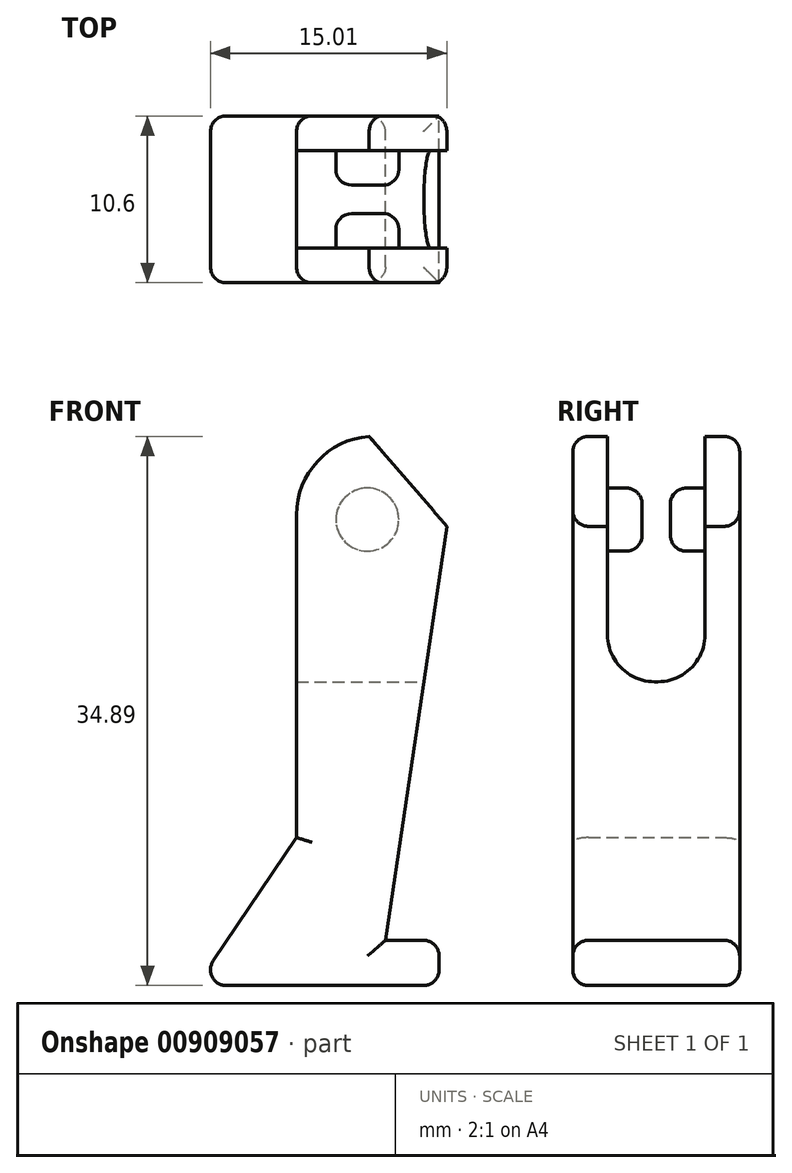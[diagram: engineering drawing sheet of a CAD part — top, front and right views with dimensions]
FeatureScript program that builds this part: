
annotation { "Feature Type Name" : "Feature", "Feature Type Description" : "" }
export const myFeature = defineFeature(function(context is Context, id is Id, definition is map)
    precondition{}
    {
        {
            var Q0;
            Q0=qCreatedBy(makeId("Front.planeOp"),FACE);
            var sketch = newSketch(context, id + "F0", { "sketchPlane" : qUnion([Q0])});
            skLineSegment(sketch, "E0", {"start": v(-7.7, 0) * mm, "end": v(7.7, 0) * mm});
            skLineSegment(sketch, "E1", {"start": v(-7.7, 0) * mm, "end": v(-1.36, 9.4) * mm});
            skLineSegment(sketch, "E2", {"start": v(-1.36, 9.4) * mm, "end": v(-1.36, 34.9) * mm});
            skLineSegment(sketch, "E3", {"start": v(-1.36, 34.9) * mm, "end": v(9.04, 34.9) * mm});
            skLineSegment(sketch, "E4", {"start": v(7.7, 0) * mm, "end": v(7.7, 2.88) * mm});
            skLineSegment(sketch, "E5", {"start": v(7.7, 2.88) * mm, "end": v(4.3, 2.88) * mm});
            skLineSegment(sketch, "E6", {"start": v(4.3, 2.88) * mm, "end": v(9.04, 34.9) * mm});
            skSolve(sketch);
        }
        {
            var Q0;
            Q0=makeQuery(id+"F0.imprint","IMPRINT",FACE,{"disambiguationData":[TD([[makeQuery(id+"F0.imprint","IMPRINT",EDGE,{"derivedFrom":sQuery(id+"F0.wireOp",EDGE,"E0")}),1.0]])]});
            extrude(context, id + "F1", {"entities" : qUnion([Q0]), "depth" : 10.6 * mm, "offsetDistance" : 25 * mm});
        }
        {
            var Q0;
            Q0=makeQuery(id+"F1.opExtrude","SWEPT_EDGE",EDGE,{"disambiguationData":[OSD([sQuery(id+"F0.wireOp",EDGE,"E2"),sQuery(id+"F0.wireOp",EDGE,"E3")])]});
            fillet(context, id + "F2", {"entities" : qUnion([Q0]), "radius" : 5 * mm, "tangentPropagation" : true, "allowEdgeOverflow" : false});
        }
        {
            var Q0;
            Q0=makeQuery(id+"F1.opExtrude","SWEPT_EDGE",EDGE,{"disambiguationData":[OSD([sQuery(id+"F0.wireOp",EDGE,"E3"),sQuery(id+"F0.wireOp",EDGE,"E6")])]});
            chamfer(context, id + "F3", {"entities" : qUnion([Q0]), "width" : 5 * mm, "tangentPropagation" : true});
        }
        {
            var Q0;
            Q0=qCreatedBy(makeId("Right.planeOp"),FACE);
            var sketch = newSketch(context, id + "F4", { "sketchPlane" : qUnion([Q0])});
            skLineSegment(sketch, "E7", {"start": v(-2.2, 34.9) * mm, "end": v(-8.4, 34.9) * mm});
            skLineSegment(sketch, "E8", {"start": v(-2.2, 34.9) * mm, "end": v(-2.2, 19.3) * mm});
            skLineSegment(sketch, "E9", {"start": v(-2.2, 19.3) * mm, "end": v(-8.4, 19.3) * mm});
            skLineSegment(sketch, "E10", {"start": v(-8.4, 19.3) * mm, "end": v(-8.4, 34.9) * mm});
            skSolve(sketch);
        }
        {
            var Q0;
            Q0=makeQuery(id+"F4.imprint","IMPRINT",FACE,{"disambiguationData":[TD([[makeQuery(id+"F4.imprint","IMPRINT",EDGE,{"derivedFrom":sQuery(id+"F4.wireOp",EDGE,"E7")}),1.0]])]});
            extrude(context, id + "F5", {"entities" : qUnion([Q0]), "operationType" : NewBodyOperationType.REMOVE, "endBound" : BoundingType.SYMMETRIC, "oppositeDirection" : true, "depth" : 25 * mm, "offsetDistance" : 25 * mm});
        }
        {
            var Q0;
            Q0=qCreatedBy(makeId("Front.planeOp"),FACE);
            cPlane(context, id + "F6", {"entities" : qUnion([Q0]), "cplaneType" : CPlaneType.OFFSET, "offset" : 5.3 * mm, "width" : 150 * mm, "height" : 150 * mm});
        }
        {
            var Q0;
            Q0=makeQuery(id+"F5.boolean.opBoolean","COPY",FACE,{"derivedFrom":makeQuery(id+"F5.opExtrude","SWEPT_FACE",FACE,{"disambiguationData":[OSD([sQuery(id+"F4.wireOp",EDGE,"E8")])]})});
            var sketch = newSketch(context, id + "F7", { "sketchPlane" : qUnion([Q0])});
            skCircle(sketch, "E11", {"center": v(3.14, 29.6) * mm, "radius": 2 * mm});
            skSolve(sketch);
        }
        {
            var Q0;
            Q0=makeQuery(id+"F7.imprint","IMPRINT",FACE,{"disambiguationData":[TD([[makeQuery(id+"F7.imprint","IMPRINT",EDGE,{"derivedFrom":sQuery(id+"F7.wireOp",EDGE,"E11")}),1.0]])]});
            extrude(context, id + "F8", {"entities" : qUnion([Q0]), "operationType" : NewBodyOperationType.ADD, "depth" : (4.4 - 2.2) * mm, "offsetDistance" : 25 * mm});
        }
        {
            var Q0;
            Q0=makeQuery(id+"F1.opExtrude","SWEPT_BODY",BODY,{"disambiguationData":[OSD([sQuery(id+"F0.wireOp",EDGE,"E0"),sQuery(id+"F0.wireOp",EDGE,"E1"),sQuery(id+"F0.wireOp",EDGE,"E2"),sQuery(id+"F0.wireOp",EDGE,"E3"),sQuery(id+"F0.wireOp",EDGE,"E4"),sQuery(id+"F0.wireOp",EDGE,"E5"),sQuery(id+"F0.wireOp",EDGE,"E6")])]});
            var Q1;
            Q1=qCreatedBy(id+"F6.planeOp",FACE);
            mirror(context, id + "F9", {"operationType" : NewBodyOperationType.ADD, "entities" : qUnion([Q0]), "mirrorPlane" : qUnion([Q1])});
        }
        {
            var Q0;
            Q0=makeQuery(id+"F9.opPattern","COPY",EDGE,{"derivedFrom":makeQuery(id+"F8.opExtrude","CAP_EDGE",EDGE,{"disambiguationData":[OSD([sQuery(id+"F7.wireOp",EDGE,"E11")])],"isStart":false}),"instanceName":"1"});
            var Q1;
            Q1=makeQuery(id+"F8.opExtrude","CAP_EDGE",EDGE,{"disambiguationData":[OSD([sQuery(id+"F7.wireOp",EDGE,"E11")])],"isStart":false});
            var Q2;
            Q2=makeQuery(id+"F1.opExtrude","CAP_EDGE",EDGE,{"disambiguationData":[OSD([sQuery(id+"F0.wireOp",EDGE,"E1")])],"isStart":true});
            var Q3;
            Q3=makeQuery(id+"F1.opExtrude","SWEPT_EDGE",EDGE,{"disambiguationData":[OSD([sQuery(id+"F0.wireOp",EDGE,"E0"),sQuery(id+"F0.wireOp",EDGE,"E1")])]});
            var Q4;
            Q4=makeQuery(id+"F1.opExtrude","CAP_EDGE",EDGE,{"disambiguationData":[OSD([sQuery(id+"F0.wireOp",EDGE,"E1")])],"isStart":false});
            var Q5;
            Q5=makeQuery(id+"F1.opExtrude","CAP_EDGE",EDGE,{"disambiguationData":[OSD([sQuery(id+"F0.wireOp",EDGE,"E2")])],"isStart":false});
            var Q6;
            Q6=makeQuery(id+"F1.opExtrude","CAP_EDGE",EDGE,{"disambiguationData":[OSD([sQuery(id+"F0.wireOp",EDGE,"E2")])],"isStart":true});
            var Q7;
            Q7=makeQuery(id+"F1.opExtrude","CAP_EDGE",EDGE,{"disambiguationData":[OSD([sQuery(id+"F0.wireOp",EDGE,"E6")])],"isStart":true});
            var Q8;
            Q8=makeQuery(id+"F1.opExtrude","CAP_EDGE",EDGE,{"disambiguationData":[OSD([sQuery(id+"F0.wireOp",EDGE,"E6")])],"isStart":false});
            var Q9;
            Q9=makeQuery(id+"F1.opExtrude","CAP_EDGE",EDGE,{"disambiguationData":[OSD([sQuery(id+"F0.wireOp",EDGE,"E5")])],"isStart":false});
            var Q10;
            Q10=makeQuery(id+"F1.opExtrude","SWEPT_EDGE",EDGE,{"disambiguationData":[OSD([sQuery(id+"F0.wireOp",EDGE,"E4"),sQuery(id+"F0.wireOp",EDGE,"E5")])]});
            var Q11;
            Q11=makeQuery(id+"F1.opExtrude","CAP_EDGE",EDGE,{"disambiguationData":[OSD([sQuery(id+"F0.wireOp",EDGE,"E5")])],"isStart":true});
            var Q12;
            Q12=makeQuery(id+"F1.opExtrude","CAP_EDGE",EDGE,{"disambiguationData":[OSD([sQuery(id+"F0.wireOp",EDGE,"E0")])],"isStart":true});
            var Q13;
            Q13=makeQuery(id+"F1.opExtrude","SWEPT_EDGE",EDGE,{"disambiguationData":[OSD([sQuery(id+"F0.wireOp",EDGE,"E0"),sQuery(id+"F0.wireOp",EDGE,"E4")])]});
            var Q14;
            Q14=makeQuery(id+"F1.opExtrude","CAP_EDGE",EDGE,{"disambiguationData":[OSD([sQuery(id+"F0.wireOp",EDGE,"E0")])],"isStart":false});
            fillet(context, id + "F10", {"entities" : qUnion([Q0, Q1, Q2, Q3, Q4, Q5, Q6, Q7, Q8, Q9, Q10, Q11, Q12, Q13, Q14]), "radius" : 1 * mm, "tangentPropagation" : true, "allowEdgeOverflow" : false});
        }
        {
            var Q0;
            Q0=makeQuery(id+"F5.boolean.opBoolean","COPY",EDGE,{"derivedFrom":makeQuery(id+"F5.opExtrude","SWEPT_EDGE",EDGE,{"disambiguationData":[OSD([sQuery(id+"F4.wireOp",EDGE,"E8"),sQuery(id+"F4.wireOp",EDGE,"E9")])]})});
            var Q1;
            Q1=makeQuery(id+"F5.boolean.opBoolean","COPY",EDGE,{"derivedFrom":makeQuery(id+"F5.opExtrude","SWEPT_EDGE",EDGE,{"disambiguationData":[OSD([sQuery(id+"F4.wireOp",EDGE,"E9"),sQuery(id+"F4.wireOp",EDGE,"E10")])]})});
            fillet(context, id + "F11", {"entities" : qUnion([Q0, Q1]), "radius" : 3 * mm, "tangentPropagation" : true, "allowEdgeOverflow" : false});
        }
    });
